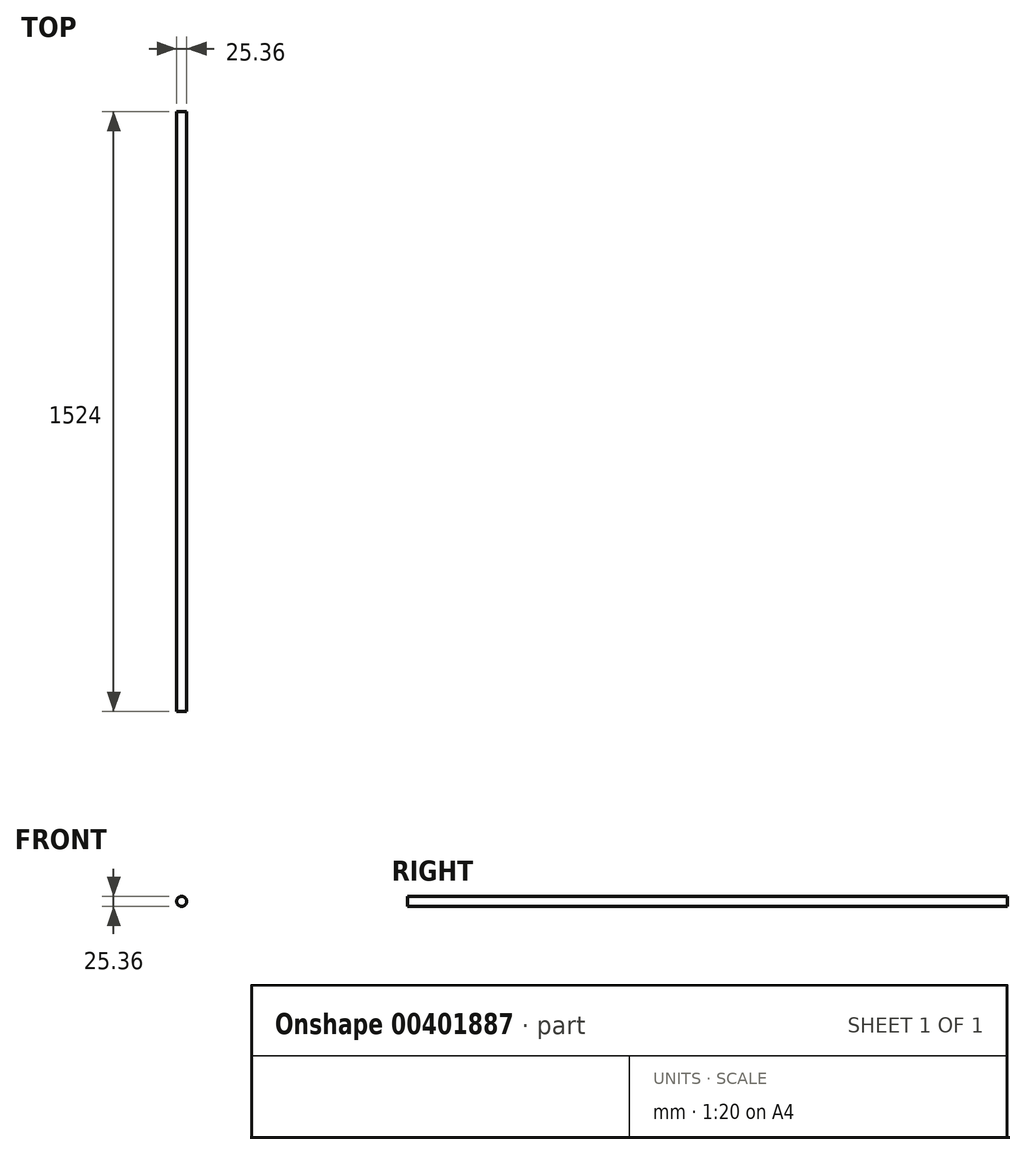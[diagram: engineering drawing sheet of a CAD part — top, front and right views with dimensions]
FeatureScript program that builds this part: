
annotation { "Feature Type Name" : "Feature", "Feature Type Description" : "" }
export const myFeature = defineFeature(function(context is Context, id is Id, definition is map)
    precondition{}
    {
        {
            var Q0;
            Q0=qCreatedBy(makeId("Front.planeOp"),FACE);
            var sketch = newSketch(context, id + "F0", { "sketchPlane" : qUnion([Q0])});
            skCircle(sketch, "E0", {"center": v(0, 0) * mm, "radius": 12.68 * mm});
            skSolve(sketch);
        }
        {
            var Q0;
            Q0=makeQuery(id+"F0.imprint","IMPRINT",FACE,{"disambiguationData":[TD([[makeQuery(id+"F0.imprint","IMPRINT",EDGE,{"derivedFrom":sQuery(id+"F0.wireOp",EDGE,"E0")}),1.0]])]});
            extrude(context, id + "F1", {"entities" : qUnion([Q0]), "depth" : 1524 * mm});
        }
    });
